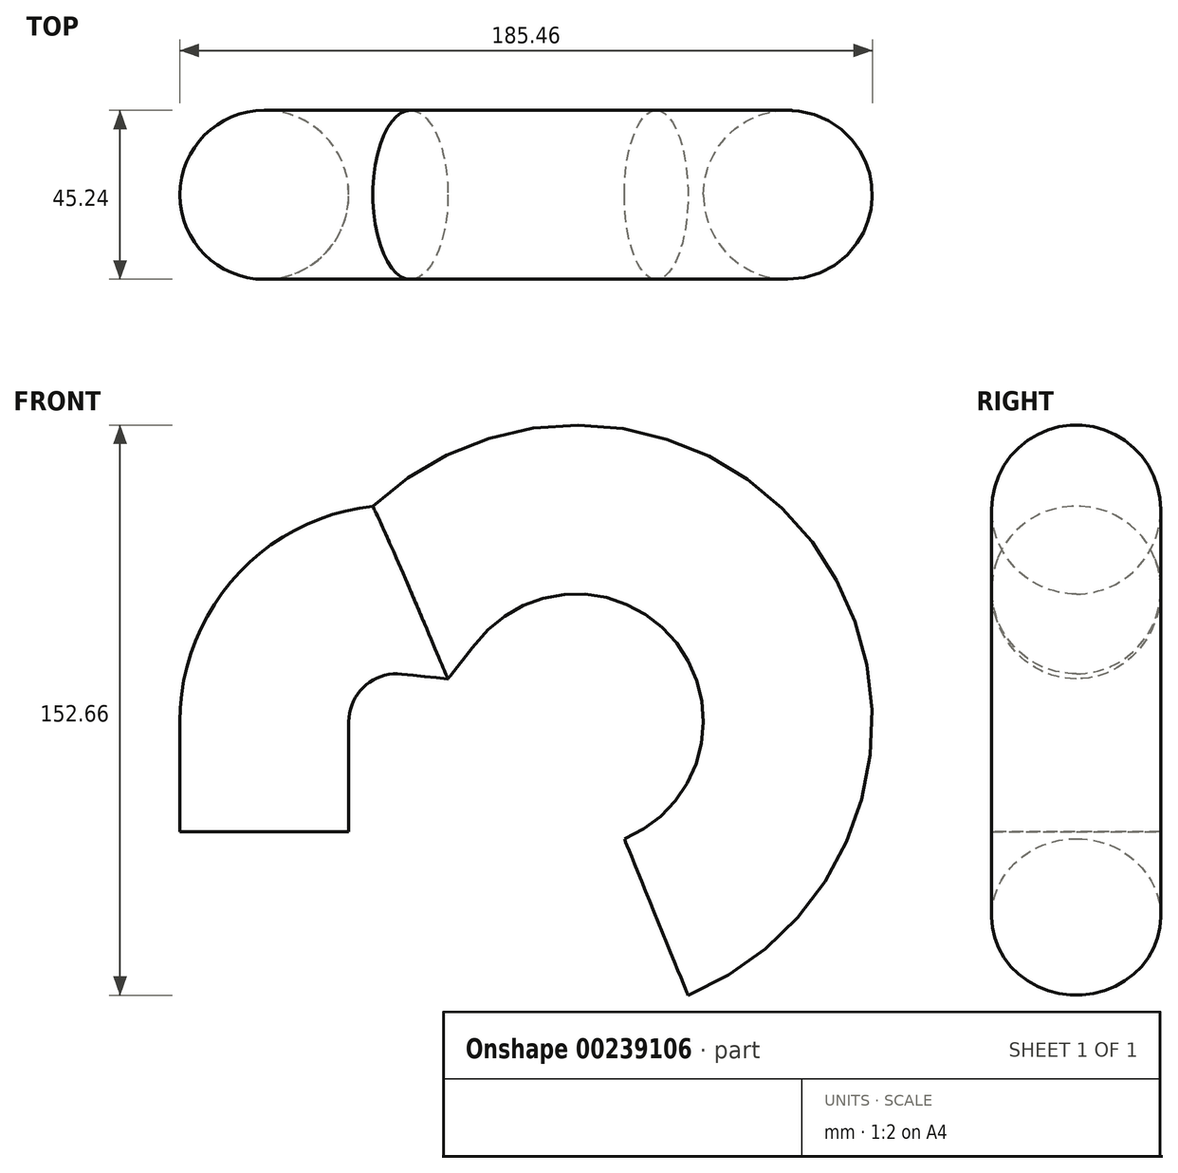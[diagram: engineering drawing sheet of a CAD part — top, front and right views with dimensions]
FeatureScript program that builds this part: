
annotation { "Feature Type Name" : "Feature", "Feature Type Description" : "" }
export const myFeature = defineFeature(function(context is Context, id is Id, definition is map)
    precondition{}
    {
        {
            var Q0;
            Q0=qCreatedBy(makeId("Front.planeOp"),FACE);
            var sketch = newSketch(context, id + "F0", { "sketchPlane" : qUnion([Q0])});
            skLineSegment(sketch, "E0", {"start": v(0, 0) * mm, "end": v(0, 29.43) * mm});
            skArc(sketch, "E1", {"start": v(39.11, 64.67) * mm, "mid": v(11.71, 55.75) * mm, "end": v(0, 29.43) * mm});
            skArc(sketch, "E2", {"start": v(104.95, -22.85) * mm, "mid": v(128.85, 63.65) * mm, "end": v(39.11, 64.67) * mm});
            skSolve(sketch);
        }
        {
            var Q0;
            Q0=qCreatedBy(makeId("Top.planeOp"),FACE);
            var sketch = newSketch(context, id + "F1", { "sketchPlane" : qUnion([Q0])});
            skCircle(sketch, "E3", {"center": v(0, 0) * mm, "radius": 22.62 * mm});
            skSolve(sketch);
        }
        {
            var Q0;
            Q0 = qSketchRegion(id + "F1", true);
            extrude(context, id + "F2", {"entities" : qUnion([Q0]), "depth" : 25 * mm});
        }
        {
            var Q0;
            Q0=makeQuery(id+"F2.opExtrude","CAP_FACE",FACE,{"disambiguationData":[OSD([sQuery(id+"F1.wireOp",EDGE,"E3")])],"isStart":false});
            var Q1;
            Q1 = qConstructionFilter(qBodyType(qCreatedBy(id + "F0" ,EDGE), BodyType.WIRE), ConstructionObject.NO);
            sweep(context, id + "F3", {"operationType" : NewBodyOperationType.ADD, "profiles" : qUnion([Q0]), "path" : qUnion([Q1])});
        }
    });
